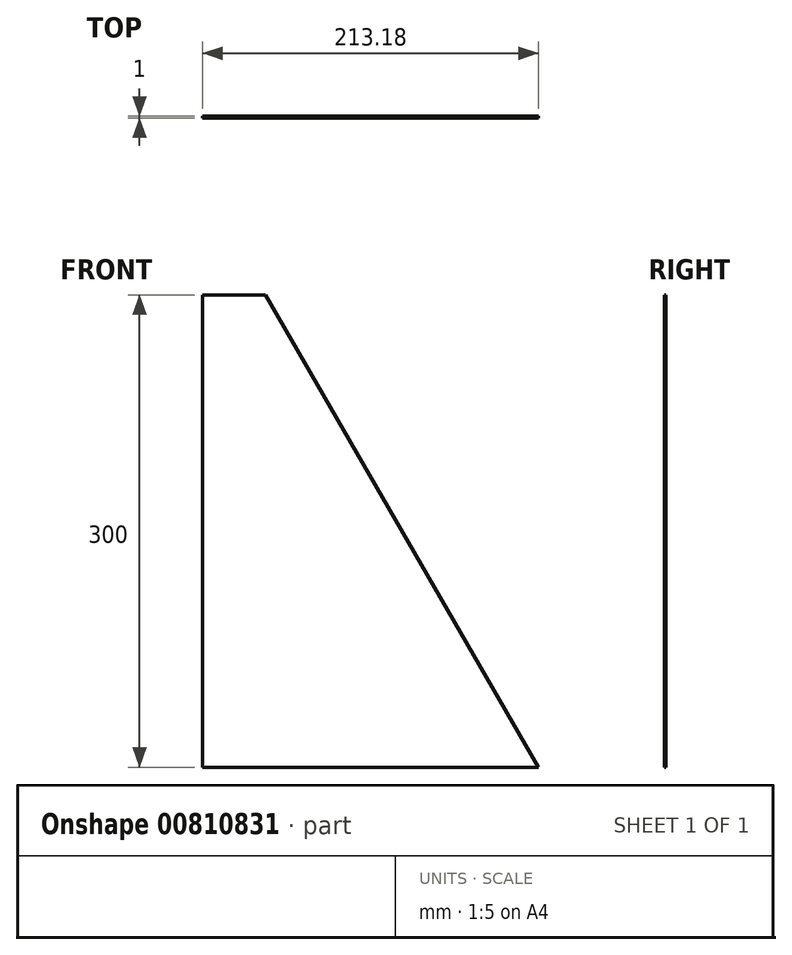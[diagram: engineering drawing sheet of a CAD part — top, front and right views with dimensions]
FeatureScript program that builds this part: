
annotation { "Feature Type Name" : "Feature", "Feature Type Description" : "" }
export const myFeature = defineFeature(function(context is Context, id is Id, definition is map)
    precondition{}
    {
        {
            var Q0;
            Q0=qCreatedBy(makeId("Front.planeOp"),FACE);
            var sketch = newSketch(context, id + "F0", { "sketchPlane" : qUnion([Q0])});
            skLineSegment(sketch, "E0", {"start": v(213.18, 0) * mm, "end": v(0, 0) * mm});
            skLineSegment(sketch, "E1", {"start": v(0, 0) * mm, "end": v(0, 300) * mm});
            skLineSegment(sketch, "E2", {"start": v(0, 300) * mm, "end": v(40, 300) * mm});
            skLineSegment(sketch, "E3", {"start": v(40, 300) * mm, "end": v(213.18, 0) * mm});
            skSolve(sketch);
        }
        {
            var Q0;
            Q0 = qSketchRegion(id + "F0", true);
            extrude(context, id + "F1", {"entities" : qUnion([Q0]), "depth" : 1 * mm, "offsetDistance" : 25 * mm});
        }
    });
